# Revit family: Door-Roll-Up-Woodfold-Lintel-Mount
name_source: partatom
category: Doors
units: mm (PartAtom-declared; Revit-internal decimal feet)

## family parameters
Always vertical = Yes
Classification Number = 23.30.10.17.27.11
Cut with Voids When Loaded = No
Host = Wall
Room Calculation Point = No
Shared = No

## types (1)
- 144" x 96"-Exterior Right Mounted Motor
    Air Leakage = 0
    Appear In Schedule = Yes
    Assembly Code = B2030420
    CTRL End Panel Depth = 0' - 6"
    CTRL Height = 8' - 0"
    CTRL Operator Width = 12' - 3"
    CTRL Rail Height = 9' - 0 1/4"
    CTRL Rail Offset from Opening = 12' - 10"
    CTRL Width = 12' - 0"
    Crank Gear Type = Crank Gear : Motorized
    Description = Woodfold Lintel Mount Roll Up Door
    Fascia Material = Wood - Veneers
    Frame Finish = Wood - Woodfold - Birch
    Frame Type = R-002 : Motorized Packout
    Frame Width = 0' - 2"
    Function = Exterior
    Has Hand Crank Packout Filler = No
    Has Left Mounted Motor = No
    Has Motorized Packout Filler = Yes
    Has Right Mounted Motor = Yes
    Height = 8' - 0"
    Manufacturer = Woodfold Mfg., Inc.
    Model = Lintel Mount Roll Up Door
    Operator Offset from Top = 1' - 0 1/4"
    Panel Material = Wood - Woodfold - Birch - Slats
    Product Documentation Link = http://woodfold.com
    Product Page URL = http://woodfold.com
    R Value = 0
    Solar Heat Gain Coefficient = 0
    Thickness = 0' - 1 3/4"
    U Value = 0
    URL = http://woodfold.com
    Visible Light Transmission = 0
    Width = 12' - 0"

## geometry (parser evidence)
native form markers: Blend x40, Sweep x24
no freeform markers — native parametric forms only
